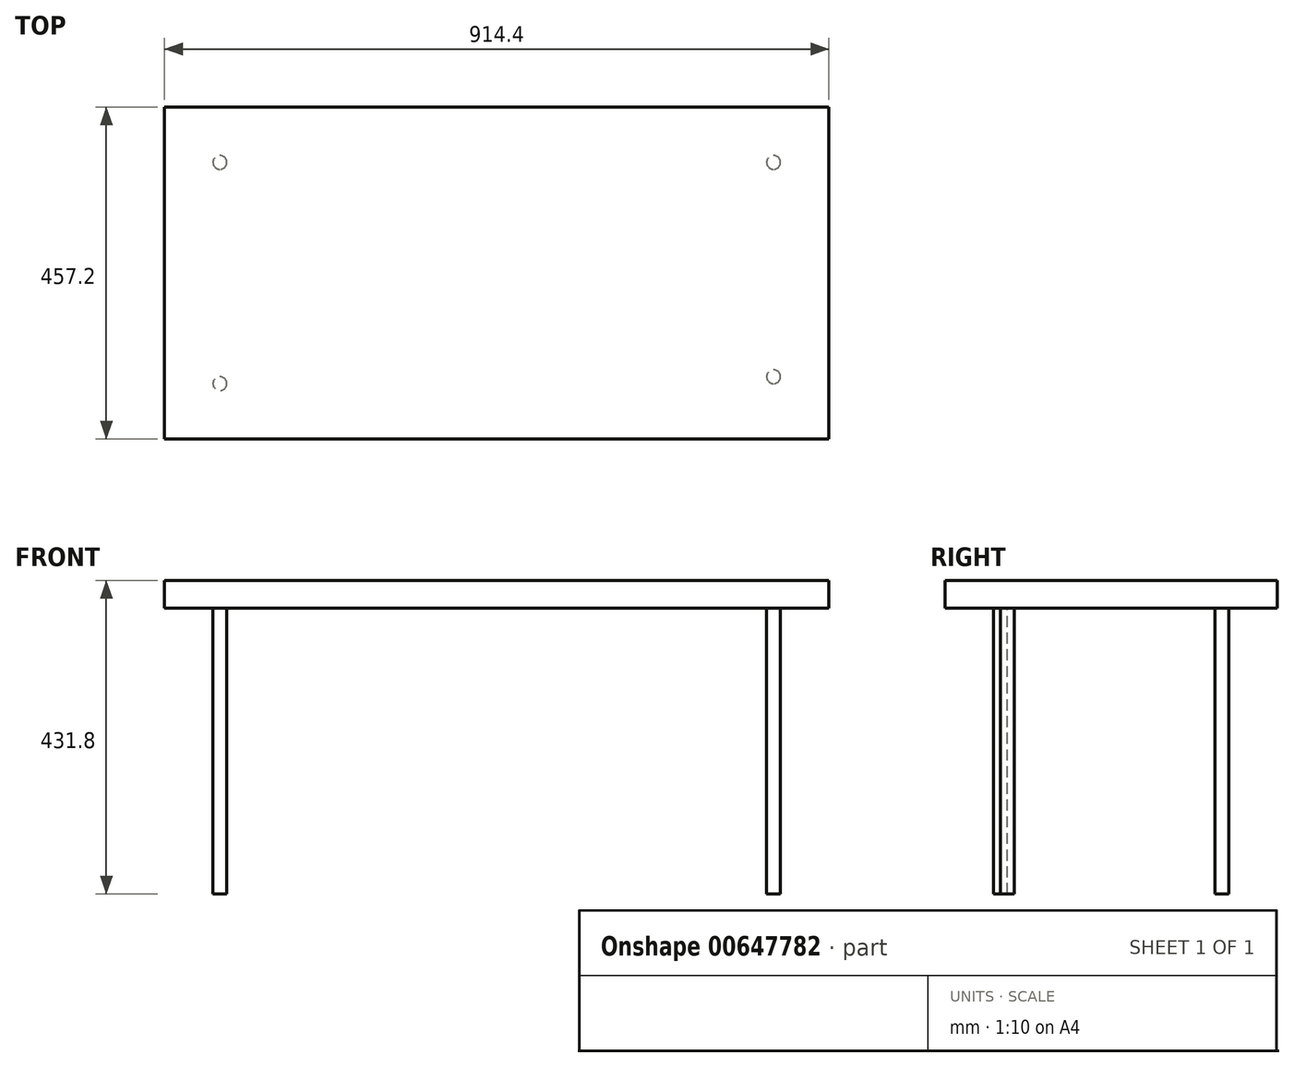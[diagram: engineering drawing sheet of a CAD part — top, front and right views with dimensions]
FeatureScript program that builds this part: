
annotation { "Feature Type Name" : "Feature", "Feature Type Description" : "" }
export const myFeature = defineFeature(function(context is Context, id is Id, definition is map)
    precondition{}
    {
        {
            var Q0;
            Q0=qCreatedBy(makeId("Front.planeOp"),FACE);
            var sketch = newSketch(context, id + "F0", { "sketchPlane" : qUnion([Q0])});
            skLineSegment(sketch, "E0.bottom", {"start": v(-457.2, -19.05) * mm, "end": v(457.2, -19.05) * mm});
            skLineSegment(sketch, "E0.top", {"start": v(-457.2, 19.05) * mm, "end": v(457.2, 19.05) * mm});
            skLineSegment(sketch, "E0.left", {"start": v(-457.2, -19.05) * mm, "end": v(-457.2, 19.05) * mm});
            skLineSegment(sketch, "E0.right", {"start": v(457.2, -19.05) * mm, "end": v(457.2, 19.05) * mm});
            skPoint(sketch, "E0.middle", {"position": v(0, 0) * mm});
            skSolve(sketch);
        }
        {
            var Q0;
            Q0=makeQuery(id+"F0.imprint","IMPRINT",FACE,{"disambiguationData":[TD([[makeQuery(id+"F0.imprint","IMPRINT",EDGE,{"derivedFrom":sQuery(id+"F0.wireOp",EDGE,"E0.bottom")}),1.0]])]});
            extrude(context, id + "F1", {"entities" : qUnion([Q0]), "endBound" : BoundingType.SYMMETRIC, "depth" : 457.2 * mm, "offsetDistance" : 25.4 * mm});
        }
        {
            var Q0;
            Q0=makeQuery(id+"F1.opExtrude","SWEPT_FACE",FACE,{"disambiguationData":[OSD([sQuery(id+"F0.wireOp",EDGE,"E0.bottom")])]});
            var sketch = newSketch(context, id + "F2", { "sketchPlane" : qUnion([Q0])});
            skCircle(sketch, "E1", {"center": v(-381, 152.4) * mm, "radius": 9.53 * mm});
            skCircle(sketch, "E2", {"center": v(-381, -152.4) * mm, "radius": 9.52 * mm});
            skCircle(sketch, "E3", {"center": v(381, -152.4) * mm, "radius": 9.52 * mm});
            skCircle(sketch, "E4", {"center": v(381, 142.88) * mm, "radius": 9.52 * mm});
            skSolve(sketch);
        }
        {
            var Q0;
            Q0 = qSketchRegion(id + "F2", true);
            extrude(context, id + "F3", {"entities" : qUnion([Q0]), "operationType" : NewBodyOperationType.ADD, "depth" : 393.7 * mm, "offsetDistance" : 25.4 * mm});
        }
        {
            var Q0;
            Q0=makeQuery(id+"F3.opExtrude","CAP_FACE",FACE,{"disambiguationData":[OSD([sQuery(id+"F2.wireOp",EDGE,"E1")])],"isStart":false});
            cPlane(context, id + "F4", {"entities" : qUnion([Q0]), "cplaneType" : CPlaneType.OFFSET, "offset" : 0 * mm, "width" : 152.4 * mm, "height" : 152.4 * mm});
        }
    });
